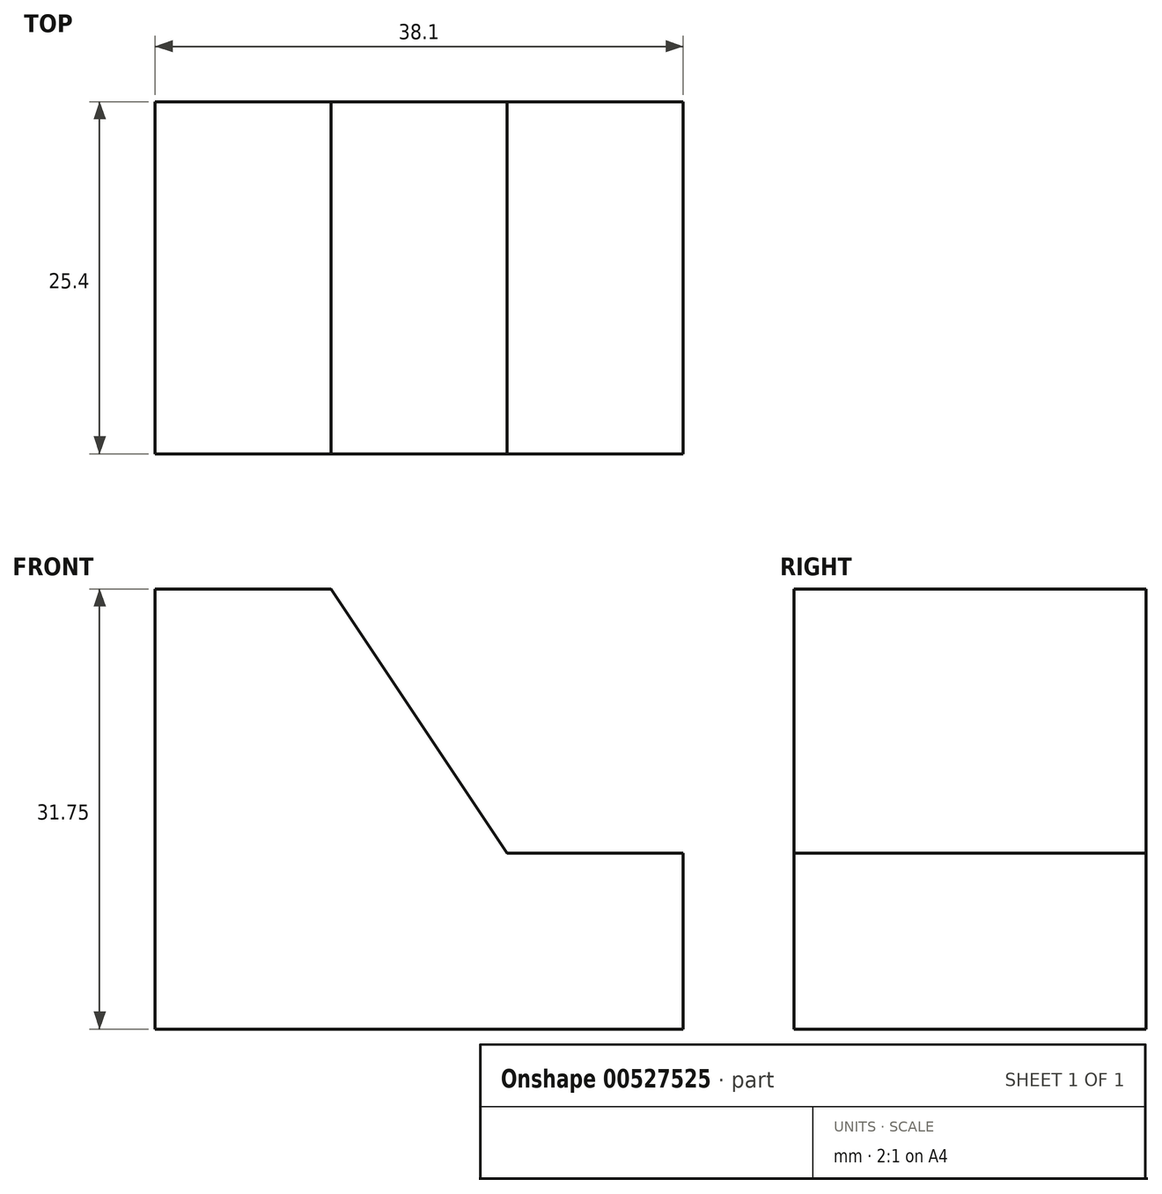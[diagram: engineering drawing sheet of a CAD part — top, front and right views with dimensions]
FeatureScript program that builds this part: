
annotation { "Feature Type Name" : "Feature", "Feature Type Description" : "" }
export const myFeature = defineFeature(function(context is Context, id is Id, definition is map)
    precondition{}
    {
        {
            var Q0;
            Q0=qCreatedBy(makeId("Front.planeOp"),FACE);
            var sketch = newSketch(context, id + "F0", { "sketchPlane" : qUnion([Q0])});
            skLineSegment(sketch, "E0", {"start": v(0, 0) * mm, "end": v(0, 31.75) * mm});
            skLineSegment(sketch, "E1", {"start": v(0, 31.75) * mm, "end": v(12.7, 31.75) * mm});
            skLineSegment(sketch, "E2", {"start": v(12.7, 31.75) * mm, "end": v(25.4, 12.7) * mm});
            skLineSegment(sketch, "E3", {"start": v(25.4, 12.7) * mm, "end": v(38.1, 12.7) * mm});
            skLineSegment(sketch, "E4", {"start": v(38.1, 12.7) * mm, "end": v(38.1, 0) * mm});
            skLineSegment(sketch, "E5", {"start": v(38.1, 0) * mm, "end": v(0, 0) * mm});
            skSolve(sketch);
        }
        {
            var Q0;
            Q0 = qSketchRegion(id + "F0", true);
            extrude(context, id + "F1", {"entities" : qUnion([Q0]), "depth" : 25.4 * mm, "offsetDistance" : 25.4 * mm});
        }
    });
